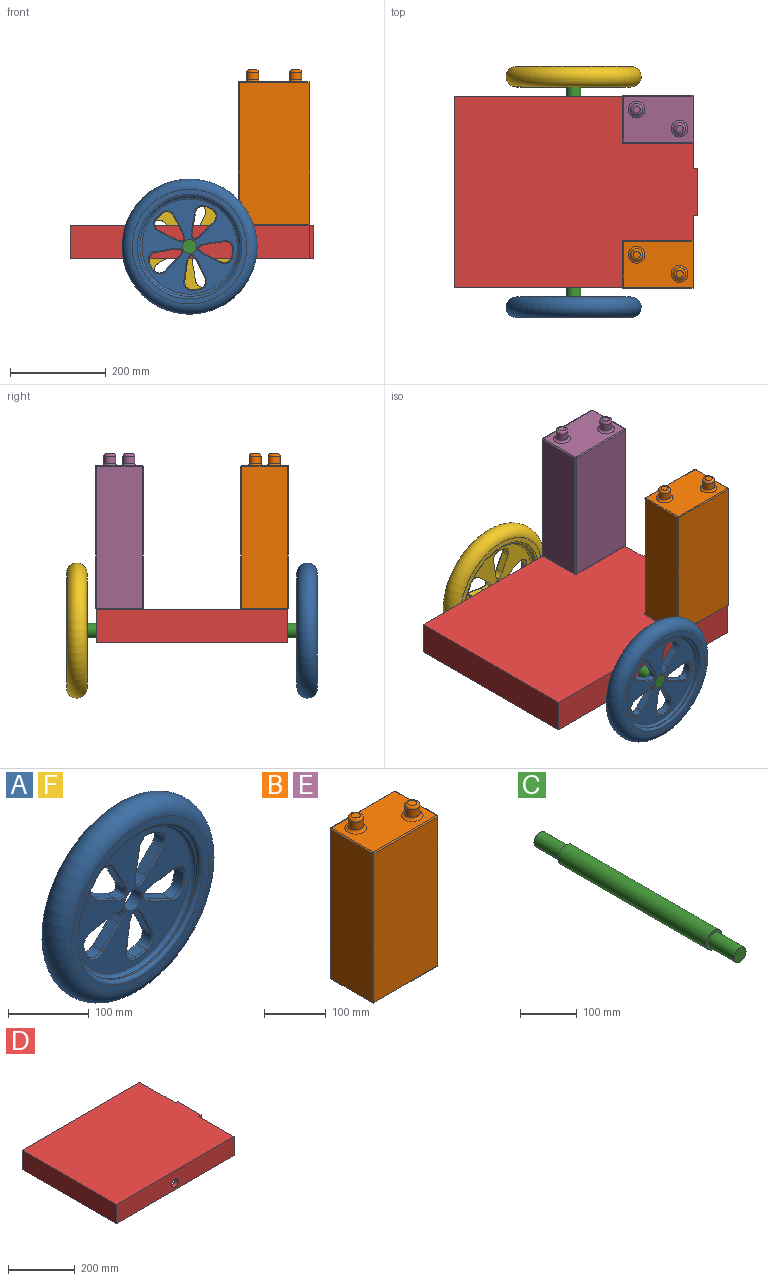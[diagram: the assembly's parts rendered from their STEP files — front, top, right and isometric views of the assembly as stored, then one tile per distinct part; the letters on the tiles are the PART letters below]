
ASSEMBLY  parts=6 mates=5
PART A: 74 faces, bbox 306.2x42.9x306.2 mm
  f0: plane 199.26x199.26mm, normal (0,-1,0), area 17920.7mm2, adj f5,f6,f41,f42,f43,f44,f45,f46
  f1: plane 199.26x199.26mm, normal (0,1,0), area 19821.7mm2, adj f6,f7,f11,f12,f13,f14,f15,f16
  f2: plane 240x240mm, normal (0,-1,0), area 7481.2mm2, adj f3,f71
  f3: torus R=109.63mm, axis (0,-1,0), area 5252.9mm2, adj f2,f4
  f4: cylinder r=104.63mm len=209.26mm, axis (0,-1,0), area 1746.4mm2, adj f3,f5
  f5: torus R=99.63mm, axis (0,-1,0), area 5073.6mm2, adj f0,f4
  f6: cylinder r=15mm len=30mm, axis (0,-1,0), area 1656.5mm2, adj f0,f1
  f7: torus R=99.63mm, axis (0,-1,0), area 5073.6mm2, adj f1,f8
  f8: cylinder r=104.63mm len=209.26mm, axis (0,-1,0), area 1746.4mm2, adj f7,f9
  f9: torus R=109.63mm, axis (0,-1,0), area 5252.9mm2, adj f8,f10
  f10: plane 240x240mm, normal (0,1,0), area 7481.2mm2, adj f9,f71
  f11: cylinder r=15mm len=21.99mm, axis (0,1,0), area 398.3mm2, adj f1,f12,f16,f70
  f12: extruded ~15.58x13.54mm, area 297.7mm2, adj f1,f11,f13,f68
  f13: cylinder r=15mm len=22.14mm, axis (0,1,0), area 401.2mm2, adj f1,f12,f14,f66
  f14: plane 35.06x18.64mm, normal (0.47,0,0.88), area 618.6mm2, adj f1,f13,f15,f65
  f15: extruded ~17.49x17.49mm, area 530.7mm2, adj f1,f14,f16,f67
  f16: plane 34.98x18.6mm, normal (-0.88,0,-0.47), area 617.1mm2, adj f1,f11,f15,f69
  f17: cylinder r=15mm len=19.33mm, axis (0,1,0), area 398.3mm2, adj f1,f18,f22,f64
  f18: extruded ~17.01x15.58mm, area 297.7mm2, adj f1,f17,f19,f62
  f19: cylinder r=15mm len=22.61mm, axis (0,1,0), area 401.2mm2, adj f1,f18,f20,f60
  f20: plane 28.57x27.59mm, normal (-0.69,0,0.72), area 618.6mm2, adj f1,f19,f21,f59
  f21: extruded ~18.04x16.44mm, area 530.7mm2, adj f1,f20,f22,f61
  f22: plane 39.02x15.58mm, normal (0.17,0,-0.98), area 617.1mm2, adj f1,f17,f21,f63
  f23: cylinder r=15mm len=17.09mm, axis (0,1,0), area 398.3mm2, adj f1,f24,f28,f58
  f24: extruded ~18.82x15.58mm, area 297.7mm2, adj f1,f23,f25,f56
  f25: cylinder r=15mm len=20.87mm, axis (0,1,0), area 401.2mm2, adj f1,f24,f26,f54
  f26: plane 35.69x17.41mm, normal (-0.9,0,-0.44), area 618.6mm2, adj f1,f25,f27,f53
  f27: extruded ~19.6x15.58mm, area 530.7mm2, adj f1,f26,f28,f55
  f28: plane 39.23x15.58mm, normal (0.99,0,-0.14), area 617.1mm2, adj f1,f23,f27,f57
  f29: cylinder r=15mm len=20.81mm, axis (0,1,0), area 398.3mm2, adj f1,f30,f34,f52
  f30: extruded ~18.78x15.58mm, area 297.7mm2, adj f1,f29,f31,f50
  f31: cylinder r=15mm len=17.09mm, axis (0,1,0), area 401.2mm2, adj f1,f30,f32,f48
  f32: plane 39.33x15.58mm, normal (0.14,0,-0.99), area 618.6mm2, adj f1,f31,f33,f47
  f33: extruded ~19.6x15.58mm, area 530.7mm2, adj f1,f32,f34,f49
  f34: plane 35.61x17.37mm, normal (0.44,0,0.9), area 617.1mm2, adj f1,f29,f33,f51
  f35: cylinder r=15mm len=22.5mm, axis (0,1,0), area 398.3mm2, adj f1,f36,f40,f46
  f36: extruded ~16.91x15.58mm, area 297.7mm2, adj f1,f35,f37,f44
  f37: cylinder r=15mm len=19.5mm, axis (0,1,0), area 401.2mm2, adj f1,f36,f38,f42
  f38: plane 39.11x15.58mm, normal (0.98,0,-0.17), area 618.6mm2, adj f1,f37,f39,f41
  f39: extruded ~18.04x16.44mm, area 530.7mm2, adj f1,f38,f40,f43
  f40: plane 28.5x27.52mm, normal (-0.72,0,0.69), area 617.1mm2, adj f1,f35,f39,f45
  f41: cylinder r=2mm len=39.53mm, axis (0.17,0,0.98), area 124.9mm2, adj f0,f38,f42,f43
  f42: torus R=17mm, axis (0,-1,0), area 84.8mm2, adj f0,f37,f41,f44
  f43: bspline ~22.55x19.19mm, area 112.8mm2, adj f0,f39,f41,f45
  f44: bspline ~21.51x12.21mm, area 60.8mm2, adj f0,f36,f42,f46
  f45: cylinder r=2mm len=29.94mm, axis (-0.69,0,-0.72), area 124.6mm2, adj f0,f40,f43,f46
  f46: torus R=17mm, axis (0,-1,0), area 84.2mm2, adj f0,f35,f44,f45
  f47: cylinder r=2mm len=39.67mm, axis (0.99,0,0.14), area 124.9mm2, adj f0,f32,f48,f49
  f48: torus R=17mm, axis (0,-1,0), area 84.8mm2, adj f0,f31,f47,f50
  f49: bspline ~23.88x17.9mm, area 112.8mm2, adj f0,f33,f47,f51
  f50: bspline ~27.3x7.14mm, area 60.8mm2, adj f0,f30,f48,f52
  f51: cylinder r=2mm len=36.55mm, axis (-0.9,0,0.44), area 124.6mm2, adj f0,f34,f49,f52
  f52: torus R=17mm, axis (0,-1,0), area 84.2mm2, adj f0,f29,f50,f51
  f53: cylinder r=2mm len=36.63mm, axis (0.44,0,-0.9), area 124.9mm2, adj f0,f26,f54,f55
  f54: torus R=17mm, axis (0,-1,0), area 84.8mm2, adj f0,f25,f53,f56
  f55: bspline ~24.19x16.87mm, area 112.8mm2, adj f0,f27,f53,f57
  f56: bspline ~27.6x5.62mm, area 60.8mm2, adj f0,f24,f54,f58
  f57: cylinder r=2mm len=39.58mm, axis (0.14,0,0.99), area 124.6mm2, adj f0,f28,f55,f58
  f58: torus R=17mm, axis (0,-1,0), area 84.2mm2, adj f0,f23,f56,f57
  f59: cylinder r=2mm len=30.01mm, axis (-0.72,0,-0.69), area 124.9mm2, adj f0,f20,f60,f61
  f60: torus R=17mm, axis (0,-1,0), area 84.8mm2, adj f0,f19,f59,f62
  f61: bspline ~22.55x19.19mm, area 112.8mm2, adj f0,f21,f59,f63
  f62: bspline ~25.6x13.35mm, area 60.8mm2, adj f0,f18,f60,f64
  f63: cylinder r=2mm len=39.43mm, axis (0.98,0,0.17), area 124.6mm2, adj f0,f22,f61,f64
  f64: torus R=17mm, axis (0,-1,0), area 84.2mm2, adj f0,f17,f62,f63
  f65: cylinder r=2mm len=36.07mm, axis (-0.88,0,0.47), area 124.9mm2, adj f0,f14,f66,f67
  f66: torus R=17mm, axis (0,-1,0), area 84.8mm2, adj f0,f13,f65,f68
  f67: bspline ~21.75x20.79mm, area 112.8mm2, adj f0,f15,f65,f69
  f68: bspline ~21.31x20.1mm, area 60.8mm2, adj f0,f12,f66,f70
  f69: cylinder r=2mm len=35.98mm, axis (0.47,0,-0.88), area 124.6mm2, adj f0,f16,f67,f70
  f70: torus R=17mm, axis (0,-1,0), area 84.2mm2, adj f0,f11,f68,f69
  f71: torus R=120mm, axis (0,1,0), area 56574.5mm2, adj f2,f10
  f72: torus R=120mm, axis (0,1,0), area 42350.3mm2, adj f73
  f73: cylinder r=120mm len=240mm, axis (0,-1,0), area 24797.7mm2, adj f72
PART B: 34 faces, bbox 150x100x325 mm
  f0: cylinder r=12.5mm len=25mm, axis (0,0,-1), area 1178.1mm2, adj f11,f12
  f1: plane 15x15mm, normal (0,0,1), area 176.7mm2, adj f11
  f2: cylinder r=12.5mm len=25mm, axis (0,0,-1), area 1178.1mm2, adj f10,f13
  f3: plane 15x15mm, normal (0,0,1), area 176.7mm2, adj f10
  f4: plane 146x96mm, normal (0,0,-1), area 14016mm2, adj f22,f27,f30,f33
  f5: plane 296x96mm, normal (1,0,0), area 28416mm2, adj f19,f28,f29,f33
  f6: plane 146x96mm, normal (0,0,1), area 12091.8mm2, adj f12,f13,f14,f18,f19,f20
  f7: plane 296x96mm, normal (-1,0,0), area 28416mm2, adj f14,f17,f21,f22
  f8: plane 296x146mm, normal (0,-1,0), area 43216mm2, adj f17,f18,f27,f28
  f9: plane 296x146mm, normal (0,1,0), area 43216mm2, adj f20,f21,f29,f30
  f10: torus R=7.5mm, axis (0,0,1), area 527.2mm2, adj f2,f3
  f11: torus R=7.5mm, axis (0,0,1), area 527.2mm2, adj f0,f1
  f12: torus R=17.5mm, axis (0,0,-1), area 706.5mm2, adj f0,f6
  f13: torus R=17.5mm, axis (0,0,-1), area 706.5mm2, adj f2,f6
  f14: cylinder r=2mm len=96mm, axis (0,-1,0), area 301.6mm2, adj f6,f7,f15,f16
  f15: sphere r=2mm, area 6.3mm2, adj f14,f17,f18
  f16: sphere r=2mm, area 6.3mm2, adj f14,f20,f21
  f17: cylinder r=2mm len=296mm, axis (0,0,1), area 929.9mm2, adj f7,f8,f15,f23
  f18: cylinder r=2mm len=146mm, axis (1,0,0), area 458.7mm2, adj f6,f8,f15,f24
  f19: cylinder r=2mm len=96mm, axis (0,1,0), area 301.6mm2, adj f5,f6,f24,f25
  f20: cylinder r=2mm len=146mm, axis (-1,0,0), area 458.7mm2, adj f6,f9,f16,f25
  f21: cylinder r=2mm len=296mm, axis (0,0,-1), area 929.9mm2, adj f7,f9,f16,f26
  f22: cylinder r=2mm len=96mm, axis (0,1,0), area 301.6mm2, adj f4,f7,f23,f26
  f23: sphere r=2mm, area 6.3mm2, adj f17,f22,f27
  f24: sphere r=2mm, area 6.3mm2, adj f18,f19,f28
  f25: sphere r=2mm, area 6.3mm2, adj f19,f20,f29
  f26: sphere r=2mm, area 6.3mm2, adj f21,f22,f30
  f27: cylinder r=2mm len=146mm, axis (-1,0,0), area 458.7mm2, adj f4,f8,f23,f31
  f28: cylinder r=2mm len=296mm, axis (0,0,-1), area 929.9mm2, adj f5,f8,f24,f31
  f29: cylinder r=2mm len=296mm, axis (0,0,1), area 929.9mm2, adj f5,f9,f25,f32
  f30: cylinder r=2mm len=146mm, axis (1,0,0), area 458.7mm2, adj f4,f9,f26,f32
  f31: sphere r=2mm, area 6.3mm2, adj f27,f28,f33
  f32: sphere r=2mm, area 6.3mm2, adj f29,f30,f33
  f33: cylinder r=2mm len=96mm, axis (0,-1,0), area 301.6mm2, adj f4,f5,f31,f32
PART C: 7 faces, bbox 40x500x40 mm
  f0: cylinder r=15mm len=65mm, axis (0,1,0), area 6126.1mm2, adj f1,f3
  f1: plane 30x30mm, normal (0,-1,0), area 706.9mm2, adj f0
  f2: cylinder r=20mm len=370mm, axis (0,1,0), area 46495.6mm2, adj f3,f4
  f3: plane 40x40mm, normal (0,-1,0), area 549.8mm2, adj f0,f2
  f4: plane 40x40mm, normal (0,1,0), area 549.8mm2, adj f2,f6
  f5: plane 30x30mm, normal (0,1,0), area 706.9mm2, adj f6
  f6: cylinder r=15mm len=65mm, axis (0,1,0), area 6126.1mm2, adj f4,f5
PART D: 17 faces, bbox 510x400x70 mm
  f0: plane 150x70mm, normal (1,0,0), area 10500mm2, adj f8,f9,f13,f15
  f1: plane 400x70mm, normal (-1,0,0), area 28000mm2, adj f2,f8,f9,f13
  f2: plane 500x70mm, normal (0,-1,0), area 34293.1mm2, adj f1,f3,f9,f11,f13
  f3: plane 150x70mm, normal (1,0,0), area 10500mm2, adj f2,f9,f13,f14
  f4: plane 370x50mm, normal (-1,0,0), area 18500mm2, adj f5,f7,f9,f12
  f5: plane 470x50mm, normal (0,1,0), area 22793.1mm2, adj f4,f6,f9,f11,f12
  f6: plane 370x50mm, normal (1,0,0), area 18500mm2, adj f5,f7,f9,f12
  f7: plane 470x50mm, normal (0,-1,0), area 22793.1mm2, adj f4,f6,f9,f10,f12
  f8: plane 500x70mm, normal (0,1,0), area 34293.1mm2, adj f0,f1,f9,f10,f13
  f9: plane 510x400mm, normal (0,0,-1), area 27100mm2, adj f0,f1,f2,f3,f4,f5,f6,f7
  f10: cylinder r=15mm len=30mm, axis (0,1,0), area 1413.7mm2, adj f7,f8
  f11: cylinder r=15mm len=30mm, axis (0,1,0), area 1413.7mm2, adj f2,f5
  f12: plane 470x370mm, normal (0,0,-1), area 173900mm2, adj f4,f5,f6,f7
  f13: plane 510x400mm, normal (0,0,1), area 201000mm2, adj f0,f1,f2,f3,f8,f14,f15,f16
  f14: plane 70x10mm, normal (0,-1,0), area 700mm2, adj f3,f9,f13,f16
  f15: plane 70x10mm, normal (0,1,0), area 700mm2, adj f0,f9,f13,f16
  f16: plane 100x70mm, normal (1,0,0), area 7000mm2, adj f9,f13,f14,f15
PART E: same geometry as B
PART F: same geometry as A
PLACE A t=(-170.2,-221.18,-75.22)mm
PLACE B t=(6.8,-131.97,119.78)mm
PLACE C t=(-170.2,20.03,-75.22)mm
PLACE D t=(-170.2,20.03,-75.22)mm
PLACE E t=(6.8,172.03,119.78)mm
PLACE F rot(axis=(1,0,0),180deg) t=(-170.2,261.24,-75.22)mm
MATE revolute F.f3 <-> C.f0  axis (0,1,0) through (-170.2,270.03,-75.22)mm
MATE revolute A.f3 <-> C.f0  axis (0,-1,0) through (-170.2,-229.97,-75.22)mm
MATE revolute D.f10 <-> C.f2  axis (0,1,0) through (-170.2,-164.97,-75.22)mm
MATE fastened B.f28 <-> D.f13  axis (0,0,-1) through (79.8,-179.97,-30.22)mm
MATE fastened E.f29 <-> D.f13  axis (0,0,-1) through (79.8,220.03,-30.22)mm
